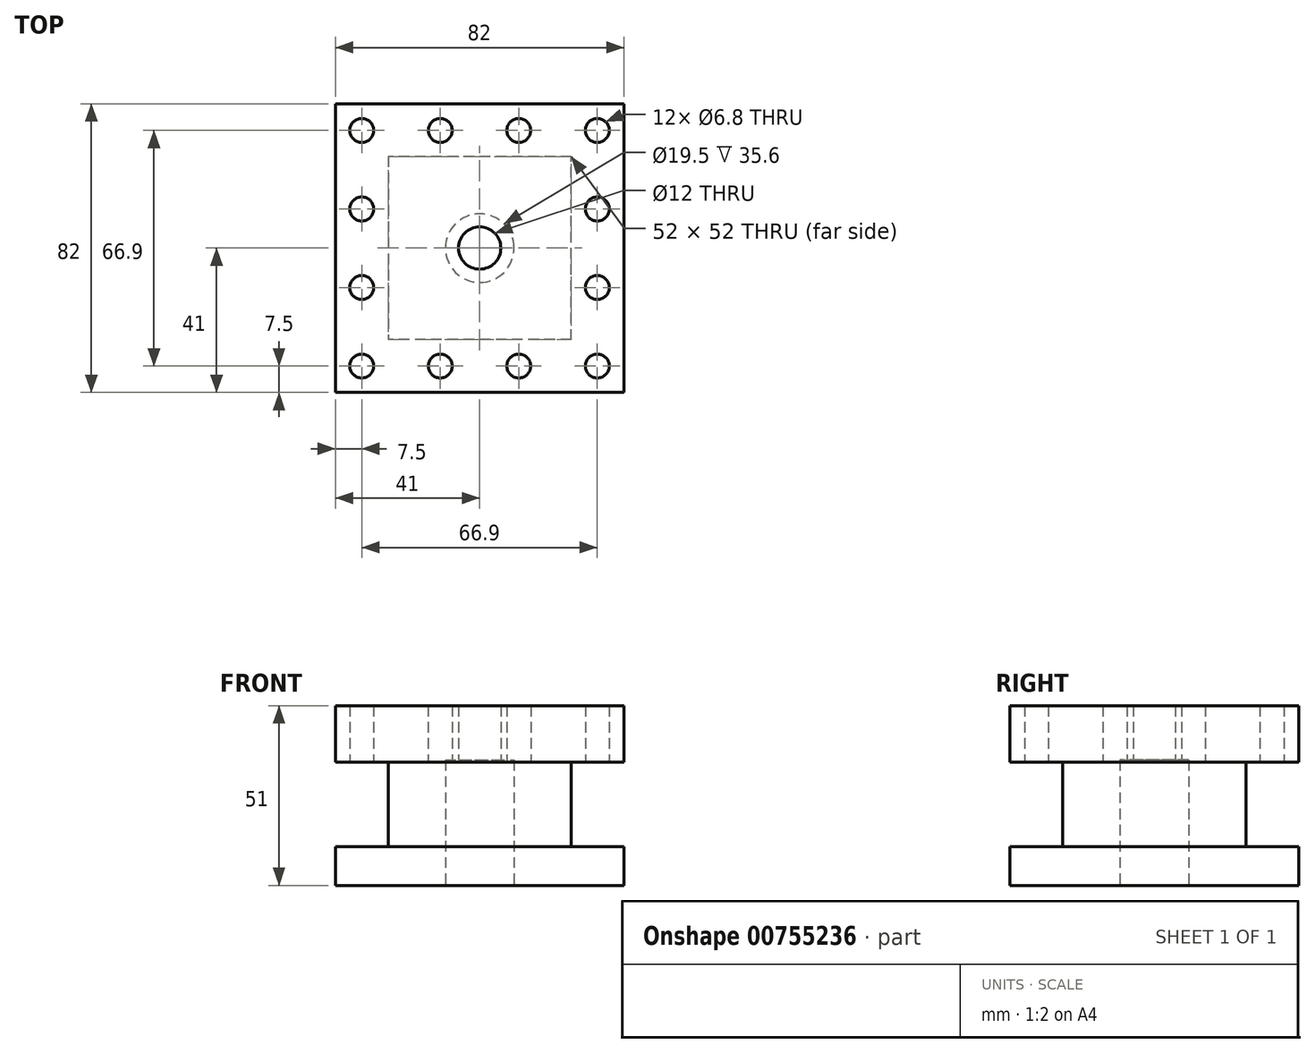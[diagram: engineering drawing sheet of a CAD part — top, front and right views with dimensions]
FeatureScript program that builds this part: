
annotation { "Feature Type Name" : "Feature", "Feature Type Description" : "" }
export const myFeature = defineFeature(function(context is Context, id is Id, definition is map)
    precondition{}
    {
        {
            var Q0;
            Q0=qCreatedBy(makeId("Right.planeOp"),FACE);
            var sketch = newSketch(context, id + "F0", { "sketchPlane" : qUnion([Q0])});
            skLineSegment(sketch, "E0", {"start": v(0, 0) * mm, "end": v(0, 11) * mm});
            skLineSegment(sketch, "E1", {"start": v(0, 11) * mm, "end": v(15, 11) * mm});
            skLineSegment(sketch, "E2", {"start": v(15, 11) * mm, "end": v(15, 35) * mm});
            skLineSegment(sketch, "E3", {"start": v(15, 35) * mm, "end": v(0, 35) * mm});
            skLineSegment(sketch, "E4", {"start": v(0, 35) * mm, "end": v(0, 51) * mm});
            skLineSegment(sketch, "E5", {"start": v(0, 51) * mm, "end": v(82, 51) * mm});
            skLineSegment(sketch, "E6", {"start": v(82, 51) * mm, "end": v(82, 35) * mm});
            skLineSegment(sketch, "E7", {"start": v(82, 35) * mm, "end": v(67, 35) * mm});
            skLineSegment(sketch, "E8", {"start": v(67, 35) * mm, "end": v(67, 11) * mm});
            skLineSegment(sketch, "E9", {"start": v(67, 11) * mm, "end": v(82, 11) * mm});
            skLineSegment(sketch, "E10", {"start": v(82, 11) * mm, "end": v(82, 0) * mm});
            skLineSegment(sketch, "E11", {"start": v(82, 0) * mm, "end": v(0, 0) * mm});
            skSolve(sketch);
        }
        {
            var Q0;
            Q0=makeQuery(id+"F0.imprint","IMPRINT",FACE,{"disambiguationData":[TD([[makeQuery(id+"F0.imprint","IMPRINT",EDGE,{"derivedFrom":sQuery(id+"F0.wireOp",EDGE,"E0")}),-1.0]])]});
            extrude(context, id + "F1", {"entities" : qUnion([Q0]), "depth" : 82 * mm, "offsetDistance" : 25 * mm});
        }
        {
            var Q0;
            Q0=makeQuery(id+"F1.opExtrude","CAP_FACE",FACE,{"disambiguationData":[OSD([sQuery(id+"F0.wireOp",EDGE,"E0"),sQuery(id+"F0.wireOp",EDGE,"E1"),sQuery(id+"F0.wireOp",EDGE,"E2"),sQuery(id+"F0.wireOp",EDGE,"E3"),sQuery(id+"F0.wireOp",EDGE,"E4"),sQuery(id+"F0.wireOp",EDGE,"E5"),sQuery(id+"F0.wireOp",EDGE,"E6"),sQuery(id+"F0.wireOp",EDGE,"E7"),sQuery(id+"F0.wireOp",EDGE,"E8"),sQuery(id+"F0.wireOp",EDGE,"E9"),sQuery(id+"F0.wireOp",EDGE,"E10"),sQuery(id+"F0.wireOp",EDGE,"E11")])],"isStart":false});
            var sketch = newSketch(context, id + "F2", { "sketchPlane" : qUnion([Q0])});
            skLineSegment(sketch, "E12", {"start": v(15, 35) * mm, "end": v(67, 35) * mm});
            skLineSegment(sketch, "E13", {"start": v(67, 35) * mm, "end": v(67, 11) * mm});
            skLineSegment(sketch, "E14", {"start": v(67, 11) * mm, "end": v(15, 11) * mm});
            skLineSegment(sketch, "E15", {"start": v(15, 11) * mm, "end": v(15, 35) * mm});
            skSolve(sketch);
        }
        {
            var Q0;
            Q0=makeQuery(id+"F2.imprint","IMPRINT",FACE,{"disambiguationData":[TD([[makeQuery(id+"F2.imprint","IMPRINT",EDGE,{"derivedFrom":sQuery(id+"F2.wireOp",EDGE,"E12")}),-1.0]])]});
            extrude(context, id + "F3", {"entities" : qUnion([Q0]), "operationType" : NewBodyOperationType.REMOVE, "oppositeDirection" : true, "depth" : 15 * mm, "offsetDistance" : 25 * mm});
        }
        {
            var Q0;
            Q0=makeQuery(id+"F1.opExtrude","CAP_FACE",FACE,{"disambiguationData":[OSD([sQuery(id+"F0.wireOp",EDGE,"E0"),sQuery(id+"F0.wireOp",EDGE,"E1"),sQuery(id+"F0.wireOp",EDGE,"E2"),sQuery(id+"F0.wireOp",EDGE,"E3"),sQuery(id+"F0.wireOp",EDGE,"E4"),sQuery(id+"F0.wireOp",EDGE,"E5"),sQuery(id+"F0.wireOp",EDGE,"E6"),sQuery(id+"F0.wireOp",EDGE,"E7"),sQuery(id+"F0.wireOp",EDGE,"E8"),sQuery(id+"F0.wireOp",EDGE,"E9"),sQuery(id+"F0.wireOp",EDGE,"E10"),sQuery(id+"F0.wireOp",EDGE,"E11")])],"isStart":true});
            var sketch = newSketch(context, id + "F4", { "sketchPlane" : qUnion([Q0])});
            skLineSegment(sketch, "E16", {"start": v(-67, 35) * mm, "end": v(-15, 35) * mm});
            skLineSegment(sketch, "E17", {"start": v(-15, 35) * mm, "end": v(-15, 11) * mm});
            skLineSegment(sketch, "E18", {"start": v(-15, 11) * mm, "end": v(-67, 11) * mm});
            skLineSegment(sketch, "E19", {"start": v(-67, 11) * mm, "end": v(-67, 35) * mm});
            skSolve(sketch);
        }
        {
            var Q0;
            Q0=makeQuery(id+"F4.imprint","IMPRINT",FACE,{"disambiguationData":[TD([[makeQuery(id+"F4.imprint","IMPRINT",EDGE,{"derivedFrom":sQuery(id+"F4.wireOp",EDGE,"E16")}),-1.0]])]});
            extrude(context, id + "F5", {"entities" : qUnion([Q0]), "operationType" : NewBodyOperationType.REMOVE, "oppositeDirection" : true, "depth" : 15 * mm, "offsetDistance" : 25 * mm});
        }
        {
            var Q0;
            Q0=makeQuery(id+"F1.opExtrude","SWEPT_FACE",FACE,{"disambiguationData":[OSD([sQuery(id+"F0.wireOp",EDGE,"E11")])]});
            var sketch = newSketch(context, id + "F6", { "sketchPlane" : qUnion([Q0])});
            skLineSegment(sketch, "E20", {"start": v(82, -41) * mm, "end": v(0, -41) * mm, "construction": true});
            skLineSegment(sketch, "E21", {"start": v(41, 0) * mm, "end": v(41, -82) * mm, "construction": true});
            skCircle(sketch, "E22", {"center": v(41, -41) * mm, "radius": 9.75 * mm});
            skSolve(sketch);
        }
        {
            var Q0;
            Q0=makeQuery(id+"F6.imprint","IMPRINT",FACE,{"disambiguationData":[TD([[makeQuery(id+"F6.imprint","IMPRINT",EDGE,{"derivedFrom":sQuery(id+"F6.wireOp",EDGE,"E22")}),1.0]])]});
            extrude(context, id + "F7", {"entities" : qUnion([Q0]), "operationType" : NewBodyOperationType.REMOVE, "oppositeDirection" : true, "depth" : 35.6 * mm, "offsetDistance" : 25 * mm});
        }
        {
            var Q0;
            Q0=makeQuery(id+"F7.boolean.opBoolean","COPY",FACE,{"derivedFrom":makeQuery(id+"F7.opExtrude","CAP_FACE",FACE,{"disambiguationData":[OSD([sQuery(id+"F6.wireOp",EDGE,"E22")])],"isStart":false})});
            var sketch = newSketch(context, id + "F8", { "sketchPlane" : qUnion([Q0])});
            skCircle(sketch, "E23", {"center": v(41, -41) * mm, "radius": 6 * mm});
            skSolve(sketch);
        }
        {
            var Q0;
            Q0=makeQuery(id+"F8.imprint","IMPRINT",FACE,{"disambiguationData":[TD([[makeQuery(id+"F8.imprint","IMPRINT",EDGE,{"derivedFrom":sQuery(id+"F8.wireOp",EDGE,"E23")}),1.0]])]});
            extrude(context, id + "F9", {"entities" : qUnion([Q0]), "operationType" : NewBodyOperationType.REMOVE, "endBound" : BoundingType.THROUGH_ALL, "oppositeDirection" : true, "depth" : 25 * mm, "offsetDistance" : 25 * mm});
        }
        {
            var Q0;
            Q0=makeQuery(id+"F1.opExtrude","SWEPT_FACE",FACE,{"disambiguationData":[OSD([sQuery(id+"F0.wireOp",EDGE,"E5")])]});
            var sketch = newSketch(context, id + "F10", { "sketchPlane" : qUnion([Q0])});
            skLineSegment(sketch, "E24", {"start": v(7.5, 0) * mm, "end": v(7.5, 82) * mm, "construction": true});
            skLineSegment(sketch, "E25", {"start": v(0, 74.5) * mm, "end": v(82, 74.5) * mm, "construction": true});
            skCircle(sketch, "E26", {"center": v(7.5, 7.5) * mm, "radius": 3.25 * mm});
            skCircle(sketch, "E27.0.1.0", {"center": v(7.5, 29.8) * mm, "radius": 3.25 * mm});
            skCircle(sketch, "E27.0.2.0", {"center": v(7.5, 52.1) * mm, "radius": 3.25 * mm});
            skCircle(sketch, "E27.0.3.0", {"center": v(7.5, 74.4) * mm, "radius": 3.25 * mm});
            skCircle(sketch, "E27.1.0.0", {"center": v(29.8, 7.5) * mm, "radius": 3.25 * mm});
            skCircle(sketch, "E27.1.3.0", {"center": v(29.8, 74.4) * mm, "radius": 3.25 * mm});
            skCircle(sketch, "E27.2.0.0", {"center": v(52.1, 7.5) * mm, "radius": 3.25 * mm});
            skCircle(sketch, "E27.2.3.0", {"center": v(52.1, 74.4) * mm, "radius": 3.25 * mm});
            skCircle(sketch, "E27.3.0.0", {"center": v(74.4, 7.5) * mm, "radius": 3.25 * mm});
            skCircle(sketch, "E27.3.1.0", {"center": v(74.4, 29.8) * mm, "radius": 3.25 * mm});
            skCircle(sketch, "E27.3.2.0", {"center": v(74.4, 52.1) * mm, "radius": 3.25 * mm});
            skCircle(sketch, "E27.3.3.0", {"center": v(74.4, 74.4) * mm, "radius": 3.25 * mm});
            skLineSegment(sketch, "E27.direction1", {"start": v(7.5, 7.5) * mm, "end": v(29.8, 7.5) * mm, "construction": true});
            skLineSegment(sketch, "E27.direction2", {"start": v(7.5, 7.5) * mm, "end": v(7.5, 29.8) * mm, "construction": true});
            skSolve(sketch);
        }
        {
            var Q0;
            Q0 = qSketchRegion(id + "F10", true);
            extrude(context, id + "F11", {"entities" : qUnion([Q0]), "operationType" : NewBodyOperationType.REMOVE, "oppositeDirection" : true, "depth" : 20 * mm, "offsetDistance" : 25 * mm});
        }
        {
            var Q0;
            Q0=sQuery(id+"F10.wireOp",VERTEX,"E26.center");
            var Q1;
            Q1=sQuery(id+"F10.wireOp",VERTEX,"E27.0.1.0.center");
            var Q2;
            Q2=sQuery(id+"F10.wireOp",VERTEX,"E27.0.2.0.center");
            var Q3;
            Q3=sQuery(id+"F10.wireOp",VERTEX,"E27.0.3.0.center");
            var Q4;
            Q4=sQuery(id+"F10.wireOp",VERTEX,"E27.1.3.0.center");
            var Q5;
            Q5=sQuery(id+"F10.wireOp",VERTEX,"E27.2.3.0.center");
            var Q6;
            Q6=sQuery(id+"F10.wireOp",VERTEX,"E27.3.3.0.center");
            var Q7;
            Q7=sQuery(id+"F10.wireOp",VERTEX,"E27.3.2.0.center");
            var Q8;
            Q8=sQuery(id+"F10.wireOp",VERTEX,"E27.3.1.0.center");
            var Q9;
            Q9=sQuery(id+"F10.wireOp",VERTEX,"E27.3.0.0.center");
            var Q10;
            Q10=sQuery(id+"F10.wireOp",VERTEX,"E27.2.0.0.center");
            var Q11;
            Q11=sQuery(id+"F10.wireOp",VERTEX,"E27.direction1.end");
            var Q12;
            Q12=makeQuery(id+"F1.opExtrude","SWEPT_BODY",BODY,{"disambiguationData":[OSD([sQuery(id+"F0.wireOp",EDGE,"E0"),sQuery(id+"F0.wireOp",EDGE,"E1"),sQuery(id+"F0.wireOp",EDGE,"E2"),sQuery(id+"F0.wireOp",EDGE,"E3"),sQuery(id+"F0.wireOp",EDGE,"E4"),sQuery(id+"F0.wireOp",EDGE,"E5"),sQuery(id+"F0.wireOp",EDGE,"E6"),sQuery(id+"F0.wireOp",EDGE,"E7"),sQuery(id+"F0.wireOp",EDGE,"E8"),sQuery(id+"F0.wireOp",EDGE,"E9"),sQuery(id+"F0.wireOp",EDGE,"E10"),sQuery(id+"F0.wireOp",EDGE,"E11")])]});
            hole(context, id + "F12", {"style" : HoleStyle.SIMPLE, "endStyle" : HoleEndStyle.BLIND, "standardTappedOrClearance" : lookupTablePath({ "standard" : "ISO", "engagement" : "75%", "pitch" : "1.25 mm", "size" : "M8", "type" : "Tapped" }), "standardBlindInLast" : lookupTablePath({ "standard" : "ISO", "engagement" : "75%", "pitch" : "1.25 mm", "size" : "M8", "type" : "Tapped" }), "holeDiameter" : 6.8 * mm, "majorDiameter" : 8 * mm, "showTappedDepth" : true, "holeDepth" : 16 * mm, "isTappedThrough" : true, "tappedDepth" : 16 * mm, "tapClearance" : 0, "locations" : qUnion([Q0, Q1, Q2, Q3, Q4, Q5, Q6, Q7, Q8, Q9, Q10, Q11]), "scope" : qUnion([Q12]), "startStyle" : HoleStartStyle.PART});
        }
    });
